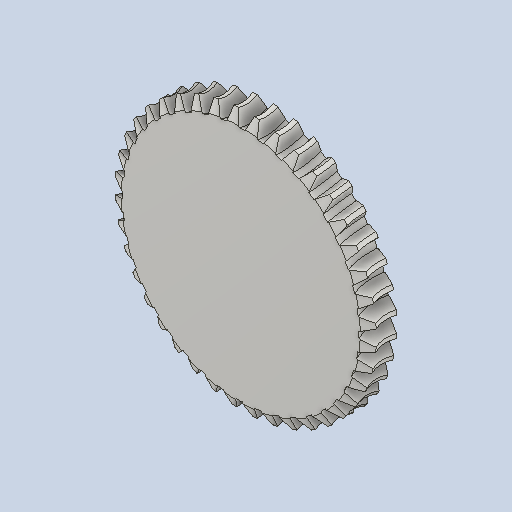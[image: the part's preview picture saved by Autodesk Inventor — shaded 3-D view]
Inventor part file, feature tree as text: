
AUTODESK INVENTOR PART (.ipt)
format: ipt  version: 2024 (Build 280153000, 153)  size: 601,600 bytes
history: native  units: mm (DEFAULTED — no unit token found)
features: other x8, plane x3, pattern_circular x1
ambient origin geometry x5: Origin, X Axis, Y Axis, Z Axis, Center Point
bodies: Solid1 (feature_tree)
feature tree (12):
  other  "Tooth Plane"
  other  "Base Body Sketch"
  other  "Base Body"
  other  "Base Body2"
  plane  "Work Plane13"
  other  "Tooth"
  pattern_circular  "Tooth Pattern"  Angle=90.0deg  [1 undecoded]
  plane  "Work Plane14"
  plane  "Work Plane15"
  other  "Tooth Sketch"
  other  "Srf1"
  other  "Pitch Diameter"
note: 1 required parameter value undecoded (feature->parameter linkage not recoverable at this tier; creation-order binding heuristic only, values carry confidence <= 0.55)
